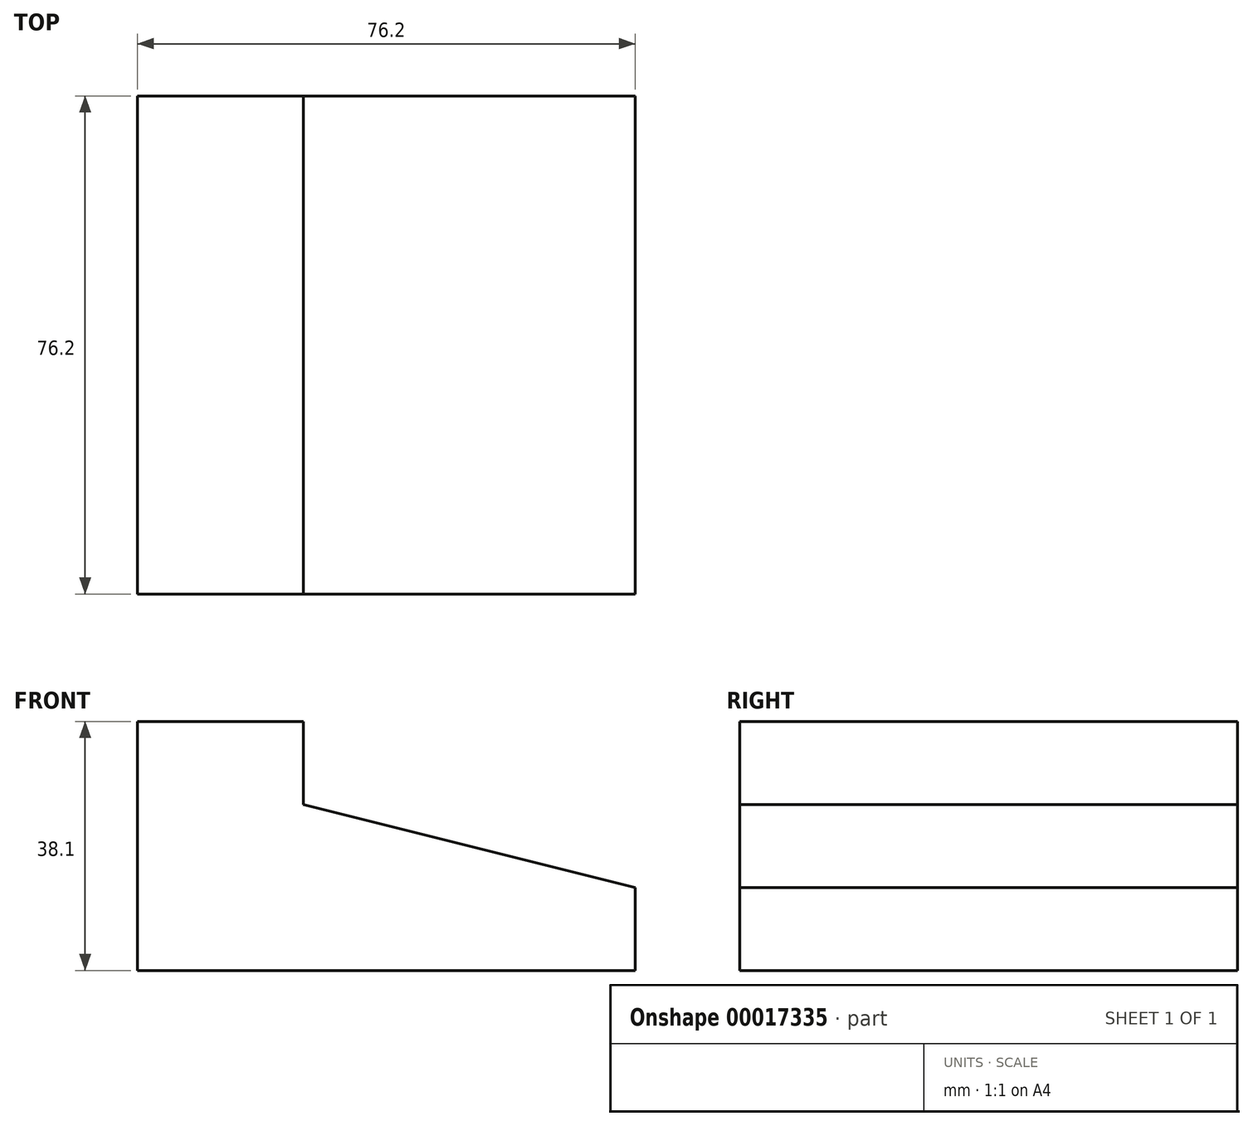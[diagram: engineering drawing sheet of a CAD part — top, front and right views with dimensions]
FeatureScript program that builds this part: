
annotation { "Feature Type Name" : "Feature", "Feature Type Description" : "" }
export const myFeature = defineFeature(function(context is Context, id is Id, definition is map)
    precondition{}
    {
        {
            var Q0;
            Q0=qCreatedBy(makeId("Front.planeOp"),FACE);
            var sketch = newSketch(context, id + "F0", { "sketchPlane" : qUnion([Q0])});
            skLineSegment(sketch, "E0", {"start": v(-71.8, 37.24) * mm, "end": v(-71.8, -0.86) * mm});
            skLineSegment(sketch, "E1", {"start": v(-71.8, -0.86) * mm, "end": v(4.4, -0.86) * mm});
            skLineSegment(sketch, "E2", {"start": v(4.4, -0.86) * mm, "end": v(4.4, 11.84) * mm});
            skLineSegment(sketch, "E3", {"start": v(4.4, 11.84) * mm, "end": v(-46.4, 24.54) * mm});
            skLineSegment(sketch, "E4", {"start": v(-46.4, 24.54) * mm, "end": v(-46.4, 37.24) * mm});
            skLineSegment(sketch, "E5", {"start": v(-46.4, 37.24) * mm, "end": v(-71.8, 37.24) * mm});
            skSolve(sketch);
        }
        {
            var Q0;
            Q0=makeQuery(id+"F0.imprint","IMPRINT",FACE,{"disambiguationData":[TD([[makeQuery(id+"F0.imprint","IMPRINT",EDGE,{"derivedFrom":sQuery(id+"F0.wireOp",EDGE,"E0")}),1.0]])]});
            extrude(context, id + "F1", {"entities" : qUnion([Q0]), "depth" : 76.2 * mm});
        }
    });
